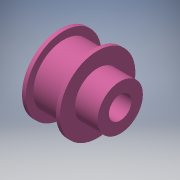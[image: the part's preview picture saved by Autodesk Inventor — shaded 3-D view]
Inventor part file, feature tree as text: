
AUTODESK INVENTOR PART (.ipt)
format: ipt  version: 2017 SP1 (Build 210196100, 196)  size: 139,264 bytes
history: native  units: in
note: dims shown in document units (in); Inventor stores cm internally (conversion verified against a paired STEP export)
features: extrude x4, sketch x4
ambient origin geometry x8: Origin, YZ Plane, XZ Plane, XY Plane, X Axis, Y Axis, Z Axis, Center Point
bodies: Solid1 (feature_tree)
feature tree (8):
  extrude  "Extrusion1"  Depth=0.375in
  extrude  "Extrusion2"  Depth=0.5in
  extrude  "Extrusion3"  Depth=0.0625in TaperAngle=0.0deg
  extrude  "Extrusion4"  Depth=0.375in TaperAngle=0.0deg
  sketch  "Sketch1"  dims[d0=1.0in d2=0.375in]
  sketch  "Sketch2"  dims[d4=0.5in d5=0.0in d6=0.125in]
  sketch  "Sketch3"  dims[d7=0.0625in d8=0.0in d9=0.0625in d10=0.0in]
  sketch  "Sketch4"  dims[d11=0.1875in d12=0.375in d13=0.0in]
